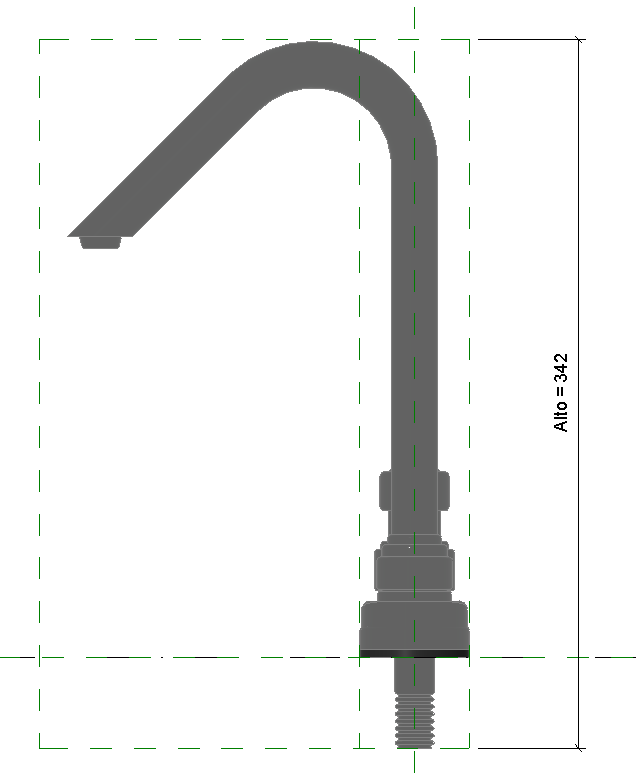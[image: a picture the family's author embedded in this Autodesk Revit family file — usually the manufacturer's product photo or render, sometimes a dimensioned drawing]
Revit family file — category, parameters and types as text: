
# Revit family: 415150001_Lavaplatos sencillo de palanca Balta
name_source: partatom
category: Plumbing Fixtures
units: mm (PartAtom-declared; Revit-internal decimal feet)

## family parameters
Cut with Voids When Loaded = No
Host = Face
OmniClass Number = 23.31.11.00
OmniClass Title = Faucets
Part Type = Normal
Room Calculation Point = No
Round Connector Dimension = Use Diameter
Shared = No

## types (1)
- Lavaplatos sencillo de palanca Balta
    Alto = 342 mm
    Ancho = 99 mm
    Capacidad de flujo máximo por norma = A 60 psi: 8.3 L/min.
    Ciclo de vida de la unidad de cierre = 500000 ciclos.
    Creado por = BIMBAU
    Default Elevation = 0 mm  [stored 0 ft]
    Description = Los acabados superficiales son aquellos que le imprimen una apariencia especial y estética a su producto y además le brindan protección. Para prolongar sus cualidades es vital que la limpieza profunda del producto se haga únicamente con agua y jabón suave y que en el secado y el brillo se utilice un paño de algodón limpio; dicha limpieza se recomienda 2 veces a la semana  y en zonas costeras a diario por la salinidad del ambiente. Por ningún motivo deben usarse elementos abrasivos, ácidos o disolventes para la limpieza del producto. Los acabados pueden variar su comportamiento en zonas costeras y/o en ambientes corrosivos
    Dimensiones generales del producto = 340 x 135 x 225 mm.
    Diámetro abasto = 13 mm  [stored 0.0426509 ft]
    Fecha de creación = 30/04/2021
    Garantía = - años.
    Manufacturer = Corona.
    Material = Corona_Plastico_Cromado
    Material 2 = Corona_Plastico_Negro
    Model = 415150001_Lavaplatos sencillo de palanca Balta
    Normatividad = NTC 1644
    Peso Bruto aprox = 435 g / 0.95 lb.
    Peso Neto aprox = 309 g / 0.68 lb
    Presion maxima = 125 psi.
    Presion minima = 20 psi.
    Profundidad = 207 mm
    Temperaturas máxima de trabajo = 5° C - 71° C.
    Vida útil = (Unidad del pico): 50000 ciclos.

note: [stored X ft] marks values corroborated as IEEE doubles in the binary element streams (Revit-internal decimal feet)

## geometry (parser evidence)
native form markers: Sweep x5
no freeform markers — native parametric forms only
